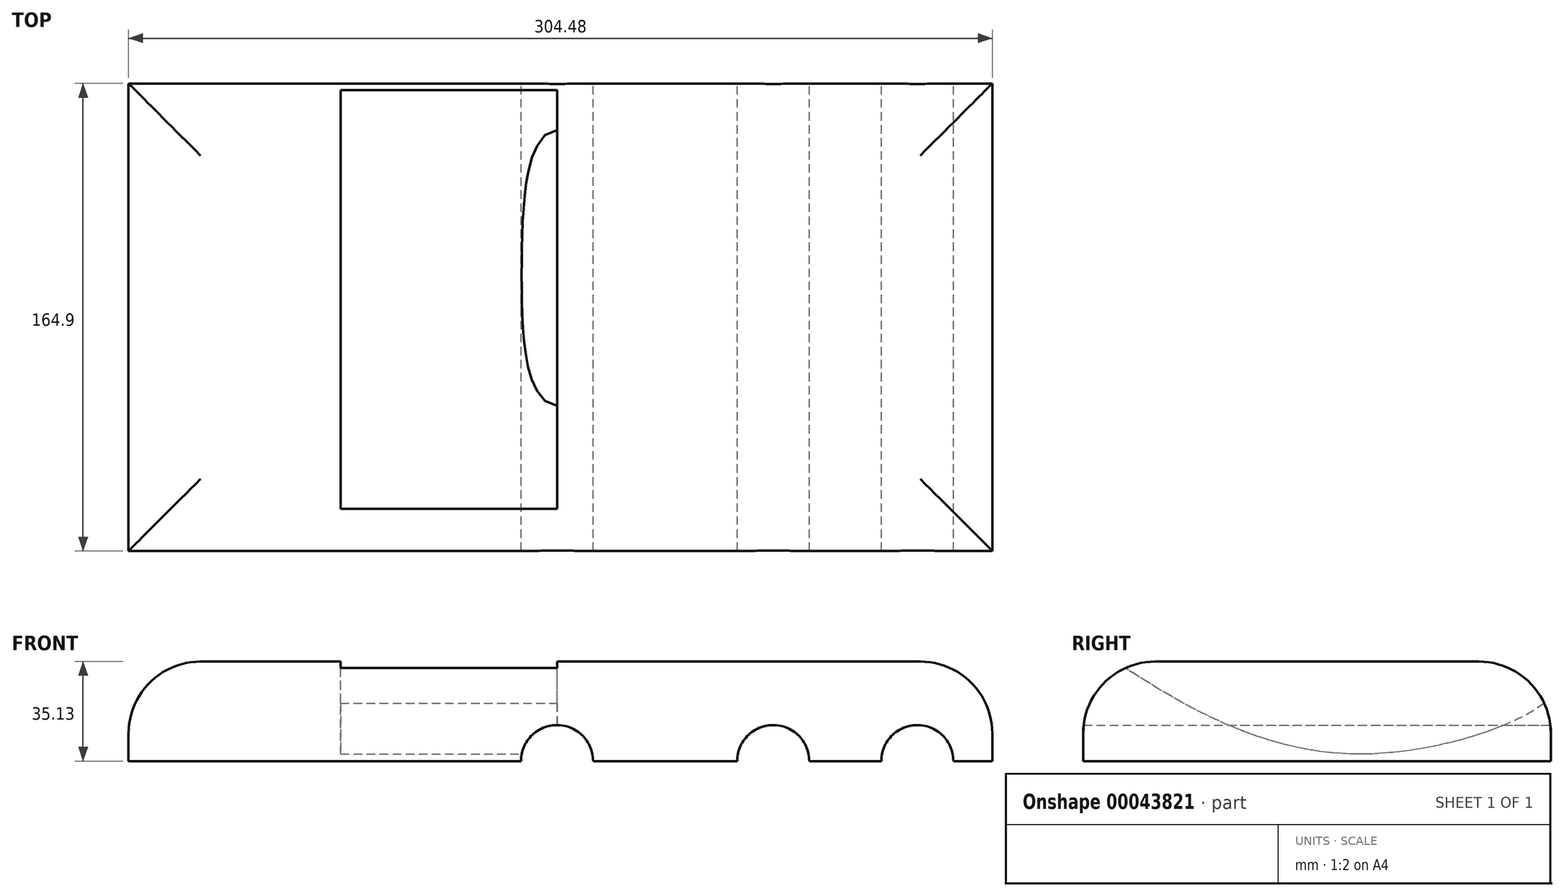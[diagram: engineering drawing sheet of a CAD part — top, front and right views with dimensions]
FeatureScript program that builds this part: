
annotation { "Feature Type Name" : "Feature", "Feature Type Description" : "" }
export const myFeature = defineFeature(function(context is Context, id is Id, definition is map)
    precondition{}
    {
        {
            var Q0;
            Q0=qCreatedBy(makeId("Top.planeOp"),FACE);
            var sketch = newSketch(context, id + "F0", { "sketchPlane" : qUnion([Q0])});
            skLineSegment(sketch, "E0.bottom", {"start": v(-151.04, 78.97) * mm, "end": v(153.44, 78.97) * mm});
            skLineSegment(sketch, "E0.top", {"start": v(-151.04, -85.93) * mm, "end": v(153.44, -85.93) * mm});
            skLineSegment(sketch, "E0.left", {"start": v(-151.04, 78.97) * mm, "end": v(-151.04, -85.93) * mm});
            skLineSegment(sketch, "E0.right", {"start": v(153.44, 78.97) * mm, "end": v(153.44, -85.93) * mm});
            skSolve(sketch);
        }
        {
            var Q0;
            Q0 = qSketchRegion(id + "F0", true);
            extrude(context, id + "F1", {"entities" : qUnion([Q0]), "depth" : 35.13 * mm});
        }
        {
            var Q0;
            Q0=qCreatedBy(makeId("Right.planeOp"),FACE);
            var sketch = newSketch(context, id + "F2", { "sketchPlane" : qUnion([Q0])});
            skFitSpline(sketch, "E1", {"points": [v(-153.2, 84.26) * mm, v(-25.7, 81.25) * mm, v(7.93, 47.36) * mm, v(80.39, 27.22) * mm, v(8.37, 2.5) * mm, v(-103.38, 54.6) * mm], "startDerivative": vector(759.46, -44.25) * mm, "endDerivative": vector(-384.18, 247.57) * mm});
            skFitSpline(sketch, "E2", {"points": [v(-153.2, 84.26) * mm, v(-103.38, 54.6) * mm], "startDerivative": vector(50.94, -21.9) * mm, "endDerivative": vector(50.94, -21.9) * mm});
            skSolve(sketch);
        }
        {
            var Q0;
            Q0 = qSketchRegion(id + "F2", true);
            extrude(context, id + "F3", {"entities" : qUnion([Q0]), "operationType" : NewBodyOperationType.REMOVE, "oppositeDirection" : true, "depth" : 76.3 * mm});
        }
        {
            var Q0;
            Q0=makeQuery(id+"F1.opExtrude","SWEPT_FACE",FACE,{"disambiguationData":[OSD([sQuery(id+"F0.wireOp",EDGE,"E0.bottom")])]});
            var sketch = newSketch(context, id + "F4", { "sketchPlane" : qUnion([Q0])});
            skCircle(sketch, "E3", {"center": v(-127, 0) * mm, "radius": 12.7 * mm});
            skCircle(sketch, "E4", {"center": v(-76.2, 0) * mm, "radius": 12.7 * mm});
            skCircle(sketch, "E5", {"center": v(0, 0) * mm, "radius": 12.7 * mm});
            skSolve(sketch);
        }
        {
            var Q0;
            Q0 = qSketchRegion(id + "F4", true);
            extrude(context, id + "F5", {"entities" : qUnion([Q0]), "operationType" : NewBodyOperationType.REMOVE, "endBound" : BoundingType.THROUGH_ALL, "oppositeDirection" : true, "depth" : 25.4 * mm});
        }
        {
            var Q0;
            Q0=makeQuery(id+"F1.opExtrude","CAP_EDGE",EDGE,{"disambiguationData":[OSD([sQuery(id+"F0.wireOp",EDGE,"E0.right")])],"isStart":false});
            var Q1;
            Q1=makeQuery(id+"F1.opExtrude","CAP_EDGE",EDGE,{"disambiguationData":[OSD([sQuery(id+"F0.wireOp",EDGE,"E0.bottom")])],"isStart":false});
            var Q2;
            Q2=makeQuery(id+"F1.opExtrude","CAP_EDGE",EDGE,{"disambiguationData":[OSD([sQuery(id+"F0.wireOp",EDGE,"E0.left")])],"isStart":false});
            var Q3;
            Q3=makeQuery(id+"F1.opExtrude","CAP_EDGE",EDGE,{"disambiguationData":[OSD([sQuery(id+"F0.wireOp",EDGE,"E0.top")])],"isStart":false});
            fillet(context, id + "F6", {"entities" : qUnion([Q0, Q1, Q2, Q3]), "radius" : 25.4 * mm, "tangentPropagation" : true, "allowEdgeOverflow" : false});
        }
    });
